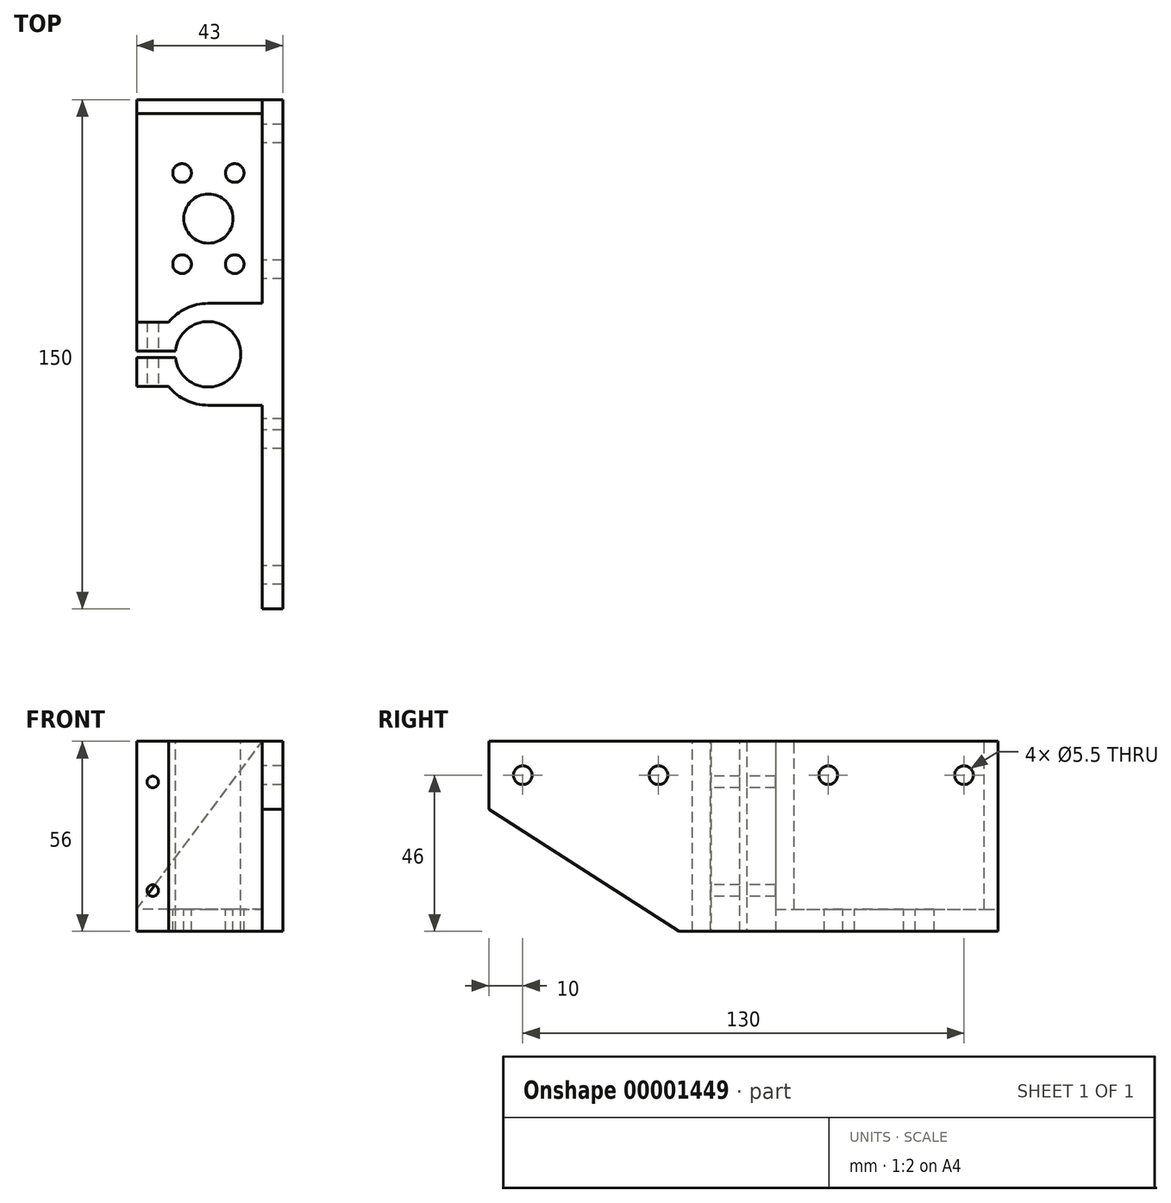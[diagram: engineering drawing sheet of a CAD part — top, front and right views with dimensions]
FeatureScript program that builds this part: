
annotation { "Feature Type Name" : "Feature", "Feature Type Description" : "" }
export const myFeature = defineFeature(function(context is Context, id is Id, definition is map)
    precondition{}
    {
        {
            var Q0;
            Q0=qCreatedBy(makeId("Top.planeOp"),FACE);
            var sketch = newSketch(context, id + "F0", { "sketchPlane" : qUnion([Q0])});
            skLineSegment(sketch, "E0", {"start": v(-160.5, 0) * mm, "end": v(160.5, 0) * mm, "construction": true});
            skLineSegment(sketch, "E1", {"start": v(-160.5, 10) * mm, "end": v(-160.5, -10) * mm, "construction": true});
            skLineSegment(sketch, "E2", {"start": v(-160.5, -10) * mm, "end": v(160.5, -10) * mm, "construction": true});
            skLineSegment(sketch, "E3", {"start": v(160.5, -10) * mm, "end": v(160.5, 10) * mm, "construction": true});
            skLineSegment(sketch, "E4", {"start": v(160.5, 10) * mm, "end": v(-160.5, 10) * mm, "construction": true});
            skLineSegment(sketch, "E5", {"start": v(-160.5, 0) * mm, "end": v(-180.5, 0) * mm, "construction": true});
            skLineSegment(sketch, "E6", {"start": v(-180.5, 180.5) * mm, "end": v(-180.5, -180.5) * mm, "construction": true});
            skLineSegment(sketch, "E7", {"start": v(-180.5, -180.5) * mm, "end": v(-160.5, -180.5) * mm, "construction": true});
            skLineSegment(sketch, "E8", {"start": v(-160.5, -180.5) * mm, "end": v(-160.5, -10) * mm, "construction": true});
            skLineSegment(sketch, "E9", {"start": v(-180.5, 180.5) * mm, "end": v(-160.5, 180.5) * mm, "construction": true});
            skLineSegment(sketch, "E10", {"start": v(-160.5, 180.5) * mm, "end": v(-160.5, 10) * mm, "construction": true});
            skLineSegment(sketch, "E11", {"start": v(0, 212.5) * mm, "end": v(0, -212.5) * mm, "construction": true});
            skLineSegment(sketch, "E12", {"start": v(-212.5, 212.5) * mm, "end": v(212.5, 212.5) * mm, "construction": true});
            skLineSegment(sketch, "E13", {"start": v(-212.5, 212.5) * mm, "end": v(-212.5, -212.5) * mm, "construction": true});
            skLineSegment(sketch, "E14", {"start": v(-212.5, -212.5) * mm, "end": v(212.5, -212.5) * mm, "construction": true});
            skLineSegment(sketch, "E15", {"start": v(212.5, -212.5) * mm, "end": v(212.5, 212.5) * mm, "construction": true});
            skLineSegment(sketch, "E16", {"start": v(-212.5, 0) * mm, "end": v(-202.5, 0) * mm, "construction": true});
            skCircle(sketch, "E17", {"center": v(-202.5, 0) * mm, "radius": 5 * mm, "construction": true});
            skLineSegment(sketch, "E18", {"start": v(-212.5, 40) * mm, "end": v(-202.4, 40) * mm, "construction": true});
            skCircle(sketch, "E19", {"center": v(-202.4, 40) * mm, "radius": 6 * mm, "construction": true});
            skSolve(sketch);
        }
        {
            var Q0;
            Q0=qCreatedBy(makeId("Top.planeOp"),FACE);
            var sketch = newSketch(context, id + "F1", { "sketchPlane" : qUnion([Q0])});
            skCircle(sketch, "E20.0", {"center": v(-202.5, 0) * mm, "radius": 5 * mm, "construction": true});
            skLineSegment(sketch, "E21.0", {"start": v(-180.5, 180.5) * mm, "end": v(-180.5, -180.5) * mm, "construction": true});
            skArc(sketch, "E22", {"start": v(-214.1, -9.5) * mm, "mid": v(-208.92, -13.56) * mm, "end": v(-202.5, -15) * mm});
            skLineSegment(sketch, "E23", {"start": v(-214.1, 9.5) * mm, "end": v(-223.5, 9.5) * mm});
            skLineSegment(sketch, "E24", {"start": v(-223.5, 9.5) * mm, "end": v(-223.5, -9.5) * mm});
            skLineSegment(sketch, "E25", {"start": v(-223.5, -9.5) * mm, "end": v(-214.1, -9.5) * mm});
            skLineSegment(sketch, "E26", {"start": v(-202.5, 15) * mm, "end": v(-180.5, 15) * mm});
            skLineSegment(sketch, "E27", {"start": v(-202.5, -15) * mm, "end": v(-180.5, -15) * mm});
            skLineSegment(sketch, "E28", {"start": v(-180.5, -15) * mm, "end": v(-180.5, 15) * mm});
            skArc(sketch, "E29.trimOffspring", {"start": v(-202.5, 15) * mm, "mid": v(-208.92, 13.56) * mm, "end": v(-214.1, 9.5) * mm});
            skLineSegment(sketch, "E30", {"start": v(-223.5, 0) * mm, "end": v(-202.5, 0) * mm, "construction": true});
            skSolve(sketch);
        }
        {
            var Q0;
            Q0=makeQuery(id+"F1.imprint","IMPRINT",FACE,{"disambiguationData":[TD([[makeQuery(id+"F1.imprint","IMPRINT",EDGE,{"derivedFrom":sQuery(id+"F1.wireOp",EDGE,"E22")}),1.0]])]});
            extrude(context, id + "F2", {"entities" : qUnion([Q0]), "depth" : 56 * mm});
        }
        {
            var Q0;
            Q0=makeQuery(id+"F2.opExtrude","CAP_FACE",FACE,{"disambiguationData":[OSD([sQuery(id+"F1.wireOp",EDGE,"E22"),sQuery(id+"F1.wireOp",EDGE,"E23"),sQuery(id+"F1.wireOp",EDGE,"E24"),sQuery(id+"F1.wireOp",EDGE,"E25"),sQuery(id+"F1.wireOp",EDGE,"E26"),sQuery(id+"F1.wireOp",EDGE,"E27"),sQuery(id+"F1.wireOp",EDGE,"E28"),sQuery(id+"F1.wireOp",EDGE,"E29.trimOffspring")])],"isStart":false});
            var sketch = newSketch(context, id + "F3", { "sketchPlane" : qUnion([Q0])});
            skLineSegment(sketch, "E31", {"start": v(-180.5, 15) * mm, "end": v(-180.5, 75) * mm});
            skLineSegment(sketch, "E32", {"start": v(-180.5, 75) * mm, "end": v(-186.5, 75) * mm});
            skLineSegment(sketch, "E33", {"start": v(-186.5, 75) * mm, "end": v(-186.5, 15) * mm});
            skLineSegment(sketch, "E34", {"start": v(-186.5, 15) * mm, "end": v(-180.5, 15) * mm});
            skLineSegment(sketch, "E35", {"start": v(-180.5, -15) * mm, "end": v(-180.5, -75) * mm});
            skLineSegment(sketch, "E36", {"start": v(-180.5, -75) * mm, "end": v(-186.5, -75) * mm});
            skLineSegment(sketch, "E37", {"start": v(-186.5, -75) * mm, "end": v(-186.5, -15) * mm});
            skLineSegment(sketch, "E38", {"start": v(-186.5, -15) * mm, "end": v(-180.5, -15) * mm});
            skLineSegment(sketch, "E39", {"start": v(-186.5, -15) * mm, "end": v(-186.5, 15) * mm, "construction": true});
            skSolve(sketch);
        }
        {
            var Q0;
            {Q0=qUnion([makeQuery(id+"F3.imprint","IMPRINT",FACE,{"disambiguationData":[TD([[makeQuery(id+"F3.imprint","IMPRINT",EDGE,{"derivedFrom":sQuery(id+"F3.wireOp",EDGE,"E31")}),1.0]])]}),makeQuery(id+"F3.imprint","IMPRINT",FACE,{"disambiguationData":[TD([[makeQuery(id+"F3.imprint","IMPRINT",EDGE,{"derivedFrom":sQuery(id+"F3.wireOp",EDGE,"E35")}),-1.0]])]})]);}
            var Q1;
            Q1=makeQuery(id+"F2.opExtrude","CAP_FACE",FACE,{"disambiguationData":[OSD([sQuery(id+"F1.wireOp",EDGE,"E22"),sQuery(id+"F1.wireOp",EDGE,"E23"),sQuery(id+"F1.wireOp",EDGE,"E24"),sQuery(id+"F1.wireOp",EDGE,"E25"),sQuery(id+"F1.wireOp",EDGE,"E26"),sQuery(id+"F1.wireOp",EDGE,"E27"),sQuery(id+"F1.wireOp",EDGE,"E28"),sQuery(id+"F1.wireOp",EDGE,"E29.trimOffspring")])],"isStart":true});
            extrude(context, id + "F4", {"entities" : qUnion([Q0]), "operationType" : NewBodyOperationType.ADD, "endBound" : BoundingType.UP_TO_SURFACE, "oppositeDirection" : true, "endBoundEntityFace" : qUnion([Q1]), "depth" : 25 * mm});
        }
        {
            var Q0;
            Q0=makeQuery(id+"F4.opExtrude","SWEPT_FACE",FACE,{"disambiguationData":[OSD([sQuery(id+"F3.wireOp",EDGE,"E32")])]});
            var sketch = newSketch(context, id + "F5", { "sketchPlane" : qUnion([Q0])});
            skLineSegment(sketch, "E40.0", {"start": v(223.5, 56) * mm, "end": v(223.5, 0) * mm, "construction": true});
            skLineSegment(sketch, "E41.bottom", {"start": v(186.5, 0) * mm, "end": v(223.5, 0) * mm});
            skLineSegment(sketch, "E41.top", {"start": v(186.5, 6.5) * mm, "end": v(223.5, 6.5) * mm});
            skLineSegment(sketch, "E41.left", {"start": v(186.5, 0) * mm, "end": v(186.5, 6.5) * mm});
            skLineSegment(sketch, "E41.right", {"start": v(223.5, 0) * mm, "end": v(223.5, 6.5) * mm});
            skSolve(sketch);
        }
        {
            var Q0;
            Q0=makeQuery(id+"F5.imprint","IMPRINT",FACE,{"disambiguationData":[TD([[makeQuery(id+"F5.imprint","IMPRINT",EDGE,{"derivedFrom":sQuery(id+"F5.wireOp",EDGE,"E41.bottom")}),1.0]])]});
            extrude(context, id + "F6", {"entities" : qUnion([Q0]), "operationType" : NewBodyOperationType.ADD, "endBound" : BoundingType.UP_TO_NEXT, "oppositeDirection" : true, "depth" : 25 * mm});
        }
        {
            var Q0;
            Q0=makeQuery(id+"F6.boolean.opBoolean","MERGE",FACE,{"derivedFrom":[makeQuery(id+"F4.opExtrude","SWEPT_FACE",FACE,{"disambiguationData":[OSD([sQuery(id+"F3.wireOp",EDGE,"E32")])]}),makeQuery(id+"F6.opExtrude","CAP_FACE",FACE,{"disambiguationData":[OSD([sQuery(id+"F5.wireOp",EDGE,"E41.bottom"),sQuery(id+"F5.wireOp",EDGE,"E41.top"),sQuery(id+"F5.wireOp",EDGE,"E41.left"),sQuery(id+"F5.wireOp",EDGE,"E41.right")])],"isStart":true})]});
            var sketch = newSketch(context, id + "F7", { "sketchPlane" : qUnion([Q0])});
            skLineSegment(sketch, "E42", {"start": v(186.5, 56) * mm, "end": v(186.5, 6.5) * mm});
            skLineSegment(sketch, "E43", {"start": v(186.5, 6.5) * mm, "end": v(223.5, 6.5) * mm});
            skLineSegment(sketch, "E44", {"start": v(223.5, 6.5) * mm, "end": v(186.5, 56) * mm});
            skSolve(sketch);
        }
        {
            var Q0;
            Q0=makeQuery(id+"F7.imprint","IMPRINT",FACE,{"disambiguationData":[TD([[makeQuery(id+"F7.imprint","IMPRINT",EDGE,{"derivedFrom":sQuery(id+"F7.wireOp",EDGE,"E42")}),-1.0]])]});
            extrude(context, id + "F8", {"entities" : qUnion([Q0]), "operationType" : NewBodyOperationType.ADD, "oppositeDirection" : true, "depth" : 4 * mm});
        }
        {
            var Q0;
            Q0=makeQuery(id+"F6.opExtrude","SWEPT_FACE",FACE,{"disambiguationData":[OSD([sQuery(id+"F5.wireOp",EDGE,"E41.top")])]});
            var sketch = newSketch(context, id + "F9", { "sketchPlane" : qUnion([Q0])});
            skCircle(sketch, "E45.0", {"center": v(-202.4, 40) * mm, "radius": 6 * mm, "construction": true});
            skCircle(sketch, "E46", {"center": v(-202.4, 40) * mm, "radius": 7.25 * mm});
            skLineSegment(sketch, "E47", {"start": v(-202.4, 40) * mm, "end": v(-210.15, 53.42) * mm, "construction": true});
            skLineSegment(sketch, "E48", {"start": v(-210.15, 53.42) * mm, "end": v(-194.65, 53.42) * mm, "construction": true});
            skLineSegment(sketch, "E49", {"start": v(-194.65, 53.42) * mm, "end": v(-202.4, 40) * mm, "construction": true});
            skLineSegment(sketch, "E50", {"start": v(-202.4, 40) * mm, "end": v(-210.15, 26.58) * mm, "construction": true});
            skLineSegment(sketch, "E51", {"start": v(-210.15, 26.58) * mm, "end": v(-194.65, 26.58) * mm, "construction": true});
            skLineSegment(sketch, "E52", {"start": v(-194.65, 26.58) * mm, "end": v(-202.4, 40) * mm, "construction": true});
            skCircle(sketch, "E53", {"center": v(-194.65, 53.42) * mm, "radius": 2.75 * mm});
            skCircle(sketch, "E54", {"center": v(-194.65, 26.58) * mm, "radius": 2.75 * mm});
            skCircle(sketch, "E55", {"center": v(-210.15, 26.58) * mm, "radius": 2.75 * mm});
            skCircle(sketch, "E56", {"center": v(-210.15, 53.42) * mm, "radius": 2.75 * mm});
            skSolve(sketch);
        }
        {
            var Q0;
            {Q0=qUnion([makeQuery(id+"F9.imprint","IMPRINT",FACE,{"disambiguationData":[TD([[makeQuery(id+"F9.imprint","IMPRINT",EDGE,{"derivedFrom":sQuery(id+"F9.wireOp",EDGE,"E46")}),1.0]])]}),makeQuery(id+"F9.imprint","IMPRINT",FACE,{"disambiguationData":[TD([[makeQuery(id+"F9.imprint","IMPRINT",EDGE,{"derivedFrom":sQuery(id+"F9.wireOp",EDGE,"E53")}),1.0]])]}),makeQuery(id+"F9.imprint","IMPRINT",FACE,{"disambiguationData":[TD([[makeQuery(id+"F9.imprint","IMPRINT",EDGE,{"derivedFrom":sQuery(id+"F9.wireOp",EDGE,"E54")}),1.0]])]}),makeQuery(id+"F9.imprint","IMPRINT",FACE,{"disambiguationData":[TD([[makeQuery(id+"F9.imprint","IMPRINT",EDGE,{"derivedFrom":sQuery(id+"F9.wireOp",EDGE,"E55")}),1.0]])]}),makeQuery(id+"F9.imprint","IMPRINT",FACE,{"disambiguationData":[TD([[makeQuery(id+"F9.imprint","IMPRINT",EDGE,{"derivedFrom":sQuery(id+"F9.wireOp",EDGE,"E56")}),1.0]])]})]);}
            extrude(context, id + "F10", {"entities" : qUnion([Q0]), "operationType" : NewBodyOperationType.REMOVE, "endBound" : BoundingType.THROUGH_ALL, "oppositeDirection" : true, "depth" : 25 * mm});
        }
        {
            var Q0;
            Q0=makeQuery(id+"F4.boolean.opBoolean","MERGE",FACE,{"derivedFrom":[makeQuery(id+"F2.opExtrude","CAP_FACE",FACE,{"disambiguationData":[OSD([sQuery(id+"F1.wireOp",EDGE,"E22"),sQuery(id+"F1.wireOp",EDGE,"E23"),sQuery(id+"F1.wireOp",EDGE,"E24"),sQuery(id+"F1.wireOp",EDGE,"E25"),sQuery(id+"F1.wireOp",EDGE,"E26"),sQuery(id+"F1.wireOp",EDGE,"E27"),sQuery(id+"F1.wireOp",EDGE,"E28"),sQuery(id+"F1.wireOp",EDGE,"E29.trimOffspring")])],"isStart":false}),makeQuery(id+"F4.opExtrude","CAP_FACE",FACE,{"disambiguationData":[OSD([sQuery(id+"F3.wireOp",EDGE,"E31"),sQuery(id+"F3.wireOp",EDGE,"E32"),sQuery(id+"F3.wireOp",EDGE,"E33"),sQuery(id+"F3.wireOp",EDGE,"E34")])],"isStart":true}),makeQuery(id+"F4.opExtrude","CAP_FACE",FACE,{"disambiguationData":[OSD([sQuery(id+"F3.wireOp",EDGE,"E35"),sQuery(id+"F3.wireOp",EDGE,"E36"),sQuery(id+"F3.wireOp",EDGE,"E37"),sQuery(id+"F3.wireOp",EDGE,"E38")])],"isStart":true})]});
            var sketch = newSketch(context, id + "F11", { "sketchPlane" : qUnion([Q0])});
            skCircle(sketch, "E57.0", {"center": v(-202.5, 0) * mm, "radius": 5 * mm, "construction": true});
            skCircle(sketch, "E58", {"center": v(-202.5, 0) * mm, "radius": 9.65 * mm});
            skSolve(sketch);
        }
        {
            var Q0;
            Q0 = qSketchRegion(id + "F11", true);
            extrude(context, id + "F12", {"entities" : qUnion([Q0]), "operationType" : NewBodyOperationType.REMOVE, "endBound" : BoundingType.THROUGH_ALL, "oppositeDirection" : true, "depth" : 25 * mm});
        }
        {
            var Q0;
            Q0=makeQuery(id+"F6.boolean.opBoolean","MERGE",FACE,{"derivedFrom":[makeQuery(id+"F2.opExtrude","SWEPT_FACE",FACE,{"disambiguationData":[OSD([sQuery(id+"F1.wireOp",EDGE,"E24")])]}),makeQuery(id+"F6.opExtrude","SWEPT_FACE",FACE,{"disambiguationData":[OSD([sQuery(id+"F5.wireOp",EDGE,"E41.right")])]})]});
            var sketch = newSketch(context, id + "F13", { "sketchPlane" : qUnion([Q0])});
            skLineSegment(sketch, "E59", {"start": v(0, 56) * mm, "end": v(0, 0) * mm, "construction": true});
            skLineSegment(sketch, "E60", {"start": v(1, 0) * mm, "end": v(1, 56) * mm});
            skLineSegment(sketch, "E61", {"start": v(-1, 56) * mm, "end": v(-1, 0) * mm});
            skLineSegment(sketch, "E62", {"start": v(-1, 0) * mm, "end": v(1, 0) * mm});
            skLineSegment(sketch, "E63", {"start": v(1, 56) * mm, "end": v(-1, 56) * mm});
            skSolve(sketch);
        }
        {
            var Q0;
            Q0 = qSketchRegion(id + "F13", true);
            var Q1;
            Q1=makeQuery(id+"F12.boolean.opBoolean","COPY",FACE,{"derivedFrom":makeQuery(id+"F12.opExtrude","SWEPT_FACE",FACE,{"disambiguationData":[OSD([sQuery(id+"F11.wireOp",EDGE,"E58")])]})});
            extrude(context, id + "F14", {"entities" : qUnion([Q0]), "operationType" : NewBodyOperationType.REMOVE, "endBound" : BoundingType.UP_TO_SURFACE, "oppositeDirection" : true, "endBoundEntityFace" : qUnion([Q1]), "depth" : 25 * mm});
        }
        {
            var Q0;
            Q0=makeQuery(id+"F2.opExtrude","SWEPT_FACE",FACE,{"disambiguationData":[OSD([sQuery(id+"F1.wireOp",EDGE,"E25")])]});
            var sketch = newSketch(context, id + "F15", { "sketchPlane" : qUnion([Q0])});
            skLineSegment(sketch, "E64", {"start": v(-218.8, 0) * mm, "end": v(-218.8, 12) * mm, "construction": true});
            skLineSegment(sketch, "E65", {"start": v(-218.8, 12) * mm, "end": v(-218.8, 44) * mm, "construction": true});
            skLineSegment(sketch, "E66", {"start": v(-218.8, 44) * mm, "end": v(-218.8, 56) * mm, "construction": true});
            skCircle(sketch, "E67", {"center": v(-218.8, 44) * mm, "radius": 1.7 * mm});
            skCircle(sketch, "E68", {"center": v(-218.8, 12) * mm, "radius": 1.7 * mm});
            skSolve(sketch);
        }
        {
            var Q0;
            {Q0=qUnion([makeQuery(id+"F15.imprint","IMPRINT",FACE,{"disambiguationData":[TD([[makeQuery(id+"F15.imprint","IMPRINT",EDGE,{"derivedFrom":sQuery(id+"F15.wireOp",EDGE,"E67")}),1.0]])]}),makeQuery(id+"F15.imprint","IMPRINT",FACE,{"disambiguationData":[TD([[makeQuery(id+"F15.imprint","IMPRINT",EDGE,{"derivedFrom":sQuery(id+"F15.wireOp",EDGE,"E68")}),1.0]])]})]);}
            var Q1;
            Q1=makeQuery(id+"F2.opExtrude","SWEPT_FACE",FACE,{"disambiguationData":[OSD([sQuery(id+"F1.wireOp",EDGE,"E23")])]});
            extrude(context, id + "F16", {"entities" : qUnion([Q0]), "operationType" : NewBodyOperationType.REMOVE, "endBound" : BoundingType.UP_TO_SURFACE, "oppositeDirection" : true, "endBoundEntityFace" : qUnion([Q1]), "depth" : 25 * mm});
        }
        {
            var Q0;
            Q0=makeQuery(id+"F4.opExtrude","SWEPT_FACE",FACE,{"disambiguationData":[OSD([sQuery(id+"F3.wireOp",EDGE,"E37")])]});
            var sketch = newSketch(context, id + "F17", { "sketchPlane" : qUnion([Q0])});
            skLineSegment(sketch, "E69", {"start": v(15, 46) * mm, "end": v(25, 46) * mm, "construction": true});
            skLineSegment(sketch, "E70", {"start": v(25, 46) * mm, "end": v(65, 46) * mm, "construction": true});
            skLineSegment(sketch, "E71", {"start": v(65, 46) * mm, "end": v(75, 46) * mm, "construction": true});
            skCircle(sketch, "E72", {"center": v(25, 46) * mm, "radius": 2.75 * mm});
            skCircle(sketch, "E73", {"center": v(65, 46) * mm, "radius": 2.75 * mm});
            skLineSegment(sketch, "E74.0.0", {"start": v(-71, 56) * mm, "end": v(-15, 56) * mm, "construction": true});
            skLineSegment(sketch, "E74.0.1", {"start": v(-71, 6.5) * mm, "end": v(-71, 56) * mm, "construction": true});
            skLineSegment(sketch, "E74.0.2", {"start": v(-15, 6.5) * mm, "end": v(-71, 6.5) * mm, "construction": true});
            skLineSegment(sketch, "E74.0.3", {"start": v(-15, 6.5) * mm, "end": v(-15, 56) * mm, "construction": true});
            skLineSegment(sketch, "E75", {"start": v(15, 46) * mm, "end": v(-15, 46) * mm, "construction": true});
            skLineSegment(sketch, "E76", {"start": v(-15, 46) * mm, "end": v(-25, 46) * mm, "construction": true});
            skLineSegment(sketch, "E77", {"start": v(-25, 46) * mm, "end": v(-65, 46) * mm, "construction": true});
            skLineSegment(sketch, "E78.0", {"start": v(-75, 6.5) * mm, "end": v(-75, 56) * mm, "construction": true});
            skLineSegment(sketch, "E79", {"start": v(-65, 46) * mm, "end": v(-75, 46) * mm, "construction": true});
            skCircle(sketch, "E80", {"center": v(-65, 46) * mm, "radius": 2.75 * mm});
            skCircle(sketch, "E81", {"center": v(-25, 46) * mm, "radius": 2.75 * mm});
            skSolve(sketch);
        }
        {
            var Q0;
            {Q0=qUnion([makeQuery(id+"F17.imprint","IMPRINT",FACE,{"disambiguationData":[TD([[makeQuery(id+"F17.imprint","IMPRINT",EDGE,{"derivedFrom":sQuery(id+"F17.wireOp",EDGE,"E80")}),1.0]])]}),makeQuery(id+"F17.imprint","IMPRINT",FACE,{"disambiguationData":[TD([[makeQuery(id+"F17.imprint","IMPRINT",EDGE,{"derivedFrom":sQuery(id+"F17.wireOp",EDGE,"E81")}),1.0]])]}),makeQuery(id+"F17.imprint","IMPRINT",FACE,{"disambiguationData":[TD([[makeQuery(id+"F17.imprint","IMPRINT",EDGE,{"derivedFrom":sQuery(id+"F17.wireOp",EDGE,"E72")}),1.0]])]}),makeQuery(id+"F17.imprint","IMPRINT",FACE,{"disambiguationData":[TD([[makeQuery(id+"F17.imprint","IMPRINT",EDGE,{"derivedFrom":sQuery(id+"F17.wireOp",EDGE,"E73")}),1.0]])]})]);}
            extrude(context, id + "F18", {"entities" : qUnion([Q0]), "operationType" : NewBodyOperationType.REMOVE, "endBound" : BoundingType.THROUGH_ALL, "oppositeDirection" : true, "depth" : 25 * mm});
        }
        {
            var Q0;
            Q0=makeQuery(id+"F4.opExtrude","SWEPT_FACE",FACE,{"disambiguationData":[OSD([sQuery(id+"F3.wireOp",EDGE,"E37")])]});
            var sketch = newSketch(context, id + "F19", { "sketchPlane" : qUnion([Q0])});
            skLineSegment(sketch, "E82", {"start": v(75, 36) * mm, "end": v(19, 0) * mm});
            skLineSegment(sketch, "E83", {"start": v(19, 0) * mm, "end": v(75, 0) * mm});
            skLineSegment(sketch, "E84", {"start": v(75, 0) * mm, "end": v(75, 36) * mm});
            skSolve(sketch);
        }
        {
            var Q0;
            Q0=makeQuery(id+"F19.imprint","IMPRINT",FACE,{"disambiguationData":[TD([[makeQuery(id+"F19.imprint","IMPRINT",EDGE,{"derivedFrom":sQuery(id+"F19.wireOp",EDGE,"E82")}),1.0]])]});
            extrude(context, id + "F20", {"entities" : qUnion([Q0]), "operationType" : NewBodyOperationType.REMOVE, "endBound" : BoundingType.THROUGH_ALL, "oppositeDirection" : true, "depth" : 25 * mm});
        }
    });
